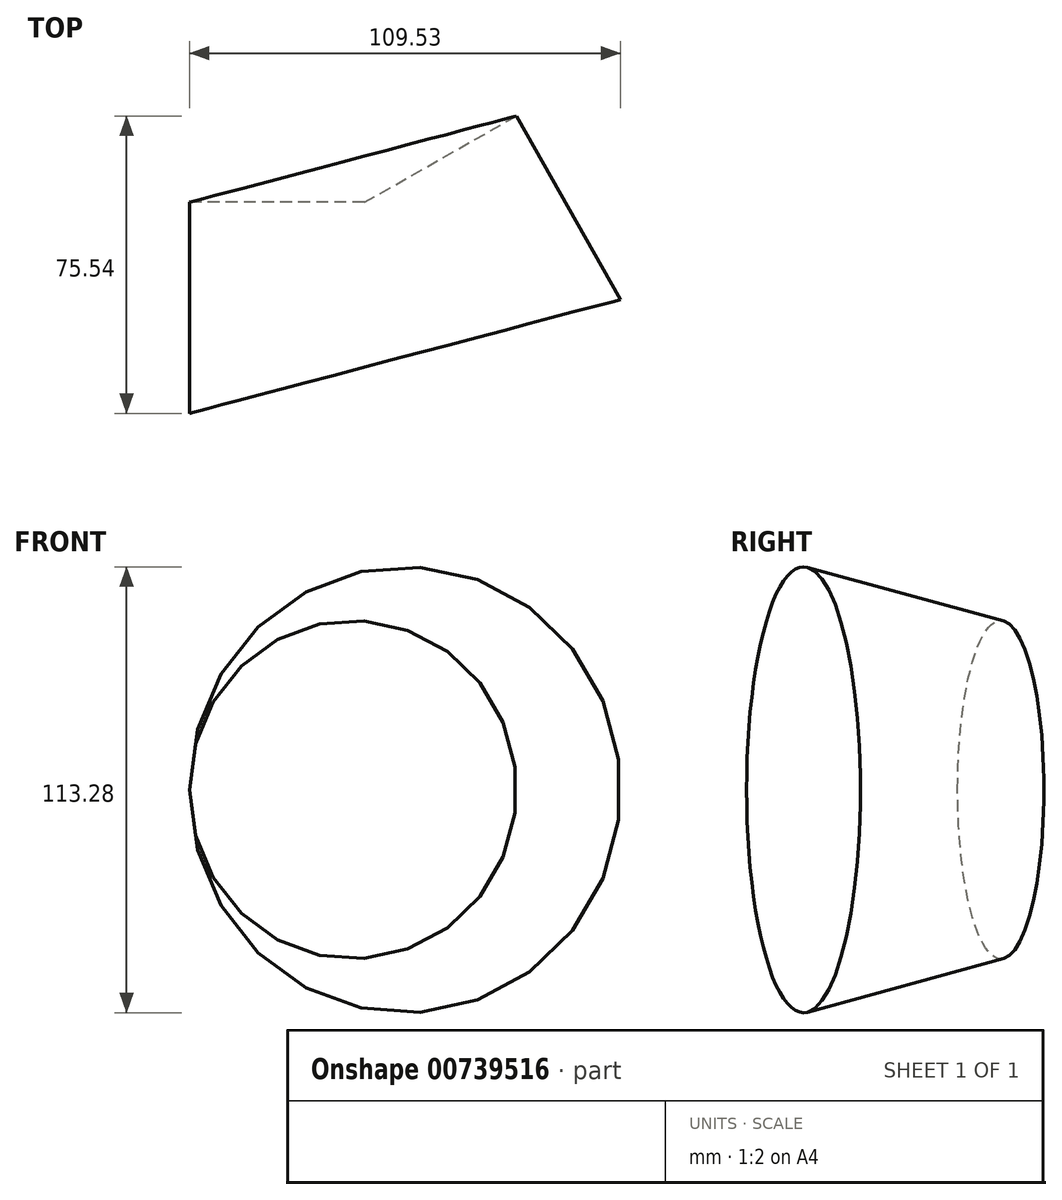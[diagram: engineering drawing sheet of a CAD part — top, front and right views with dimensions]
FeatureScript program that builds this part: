
annotation { "Feature Type Name" : "Feature", "Feature Type Description" : "" }
export const myFeature = defineFeature(function(context is Context, id is Id, definition is map)
    precondition{}
    {
        {
            var Q0;
            Q0=qCreatedBy(makeId("Top.planeOp"),FACE);
            var sketch = newSketch(context, id + "F0", { "sketchPlane" : qUnion([Q0])});
            skArc(sketch, "E0", {"start": v(92.1, 6.44) * mm, "mid": v(110.63, -53.7) * mm, "end": v(154.69, -8.76) * mm});
            skLineSegment(sketch, "E1.bottom", {"start": v(92.1, 60.05) * mm, "end": v(136.52, 60.05) * mm});
            skLineSegment(sketch, "E1.left", {"start": v(92.1, 60.05) * mm, "end": v(92.1, 6.44) * mm});
            skLineSegment(sketch, "E2", {"start": v(136.52, 60.05) * mm, "end": v(154.69, -8.76) * mm});
            skSolve(sketch);
        }
        {
            var Q0;
            Q0=makeQuery(id+"F0.imprint","IMPRINT",FACE,{"disambiguationData":[TD([[makeQuery(id+"F0.imprint","IMPRINT",EDGE,{"derivedFrom":sQuery(id+"F0.wireOp",EDGE,"E0")}),1.0]])]});
            var Q1;
            Q1=sQuery(id+"F0.wireOp",EDGE,"E2");
            revolve(context, id + "F1", {"surfaceOperationType" : NewSurfaceOperationType.NEW, "entities" : qUnion([Q0]), "axis" : qUnion([Q1]), "revolveType" : RevolveType.FULL});
        }
    });
